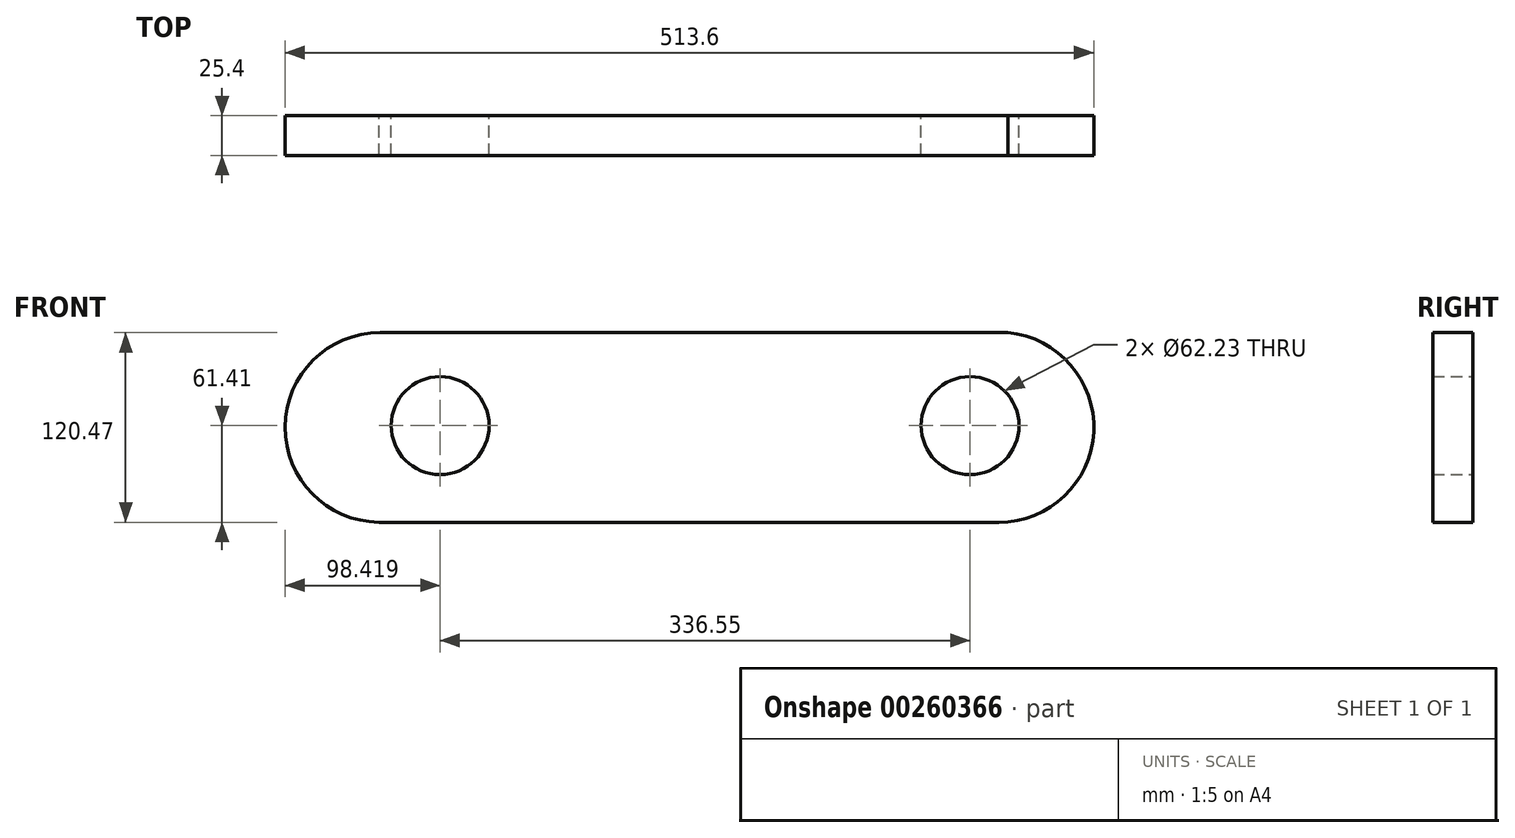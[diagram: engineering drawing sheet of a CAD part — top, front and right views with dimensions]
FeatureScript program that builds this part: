
annotation { "Feature Type Name" : "Feature", "Feature Type Description" : "" }
export const myFeature = defineFeature(function(context is Context, id is Id, definition is map)
    precondition{}
    {
        {
            var Q0;
            Q0=qCreatedBy(makeId("Front.planeOp"),FACE);
            var sketch = newSketch(context, id + "F0", { "sketchPlane" : qUnion([Q0])});
            skLineSegment(sketch, "E0", {"start": v(-66.7, 59.06) * mm, "end": v(332.08, 59.06) * mm});
            skLineSegment(sketch, "E1", {"start": v(-67.41, -61.41) * mm, "end": v(326.29, -61.41) * mm});
            skCircle(sketch, "E2", {"center": v(-28.52, 0) * mm, "radius": 31.12 * mm});
            skCircle(sketch, "E3", {"center": v(308.03, 0) * mm, "radius": 31.12 * mm});
            skArc(sketch, "E4", {"start": v(-66.7, 59.06) * mm, "mid": v(-126.94, -0.82) * mm, "end": v(-67.41, -61.41) * mm});
            skArc(sketch, "E5", {"start": v(326.29, -61.41) * mm, "mid": v(386.6, -3.93) * mm, "end": v(332.08, 59.06) * mm});
            skSolve(sketch);
        }
        {
            var Q0;
            Q0 = qSketchRegion(id + "F0", true);
            extrude(context, id + "F1", {"entities" : qUnion([Q0]), "depth" : 25.4 * mm});
        }
    });
